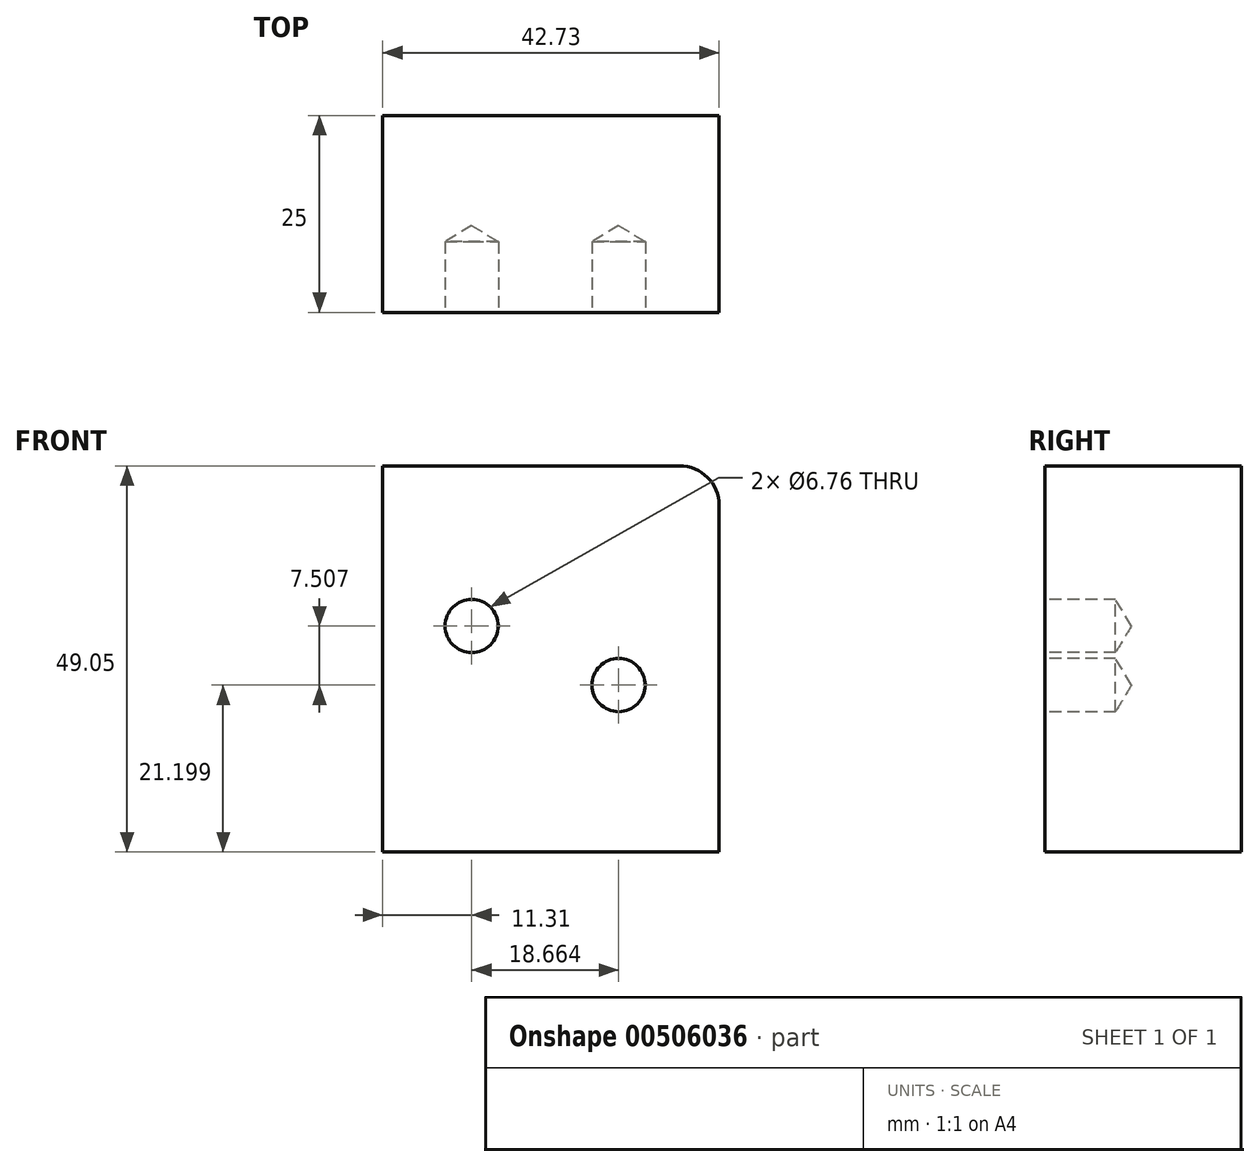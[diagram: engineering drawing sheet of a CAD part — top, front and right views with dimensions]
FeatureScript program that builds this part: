
annotation { "Feature Type Name" : "Feature", "Feature Type Description" : "" }
export const myFeature = defineFeature(function(context is Context, id is Id, definition is map)
    precondition{}
    {
        {
            var Q0;
            Q0=qCreatedBy(makeId("Front.planeOp"),FACE);
            var sketch = newSketch(context, id + "F0", { "sketchPlane" : qUnion([Q0])});
            skLineSegment(sketch, "E0.bottom", {"start": v(-90.46, 25.96) * mm, "end": v(-47.73, 25.96) * mm});
            skLineSegment(sketch, "E0.top", {"start": v(-90.46, 75) * mm, "end": v(-47.73, 75) * mm});
            skLineSegment(sketch, "E0.left", {"start": v(-90.46, 25.96) * mm, "end": v(-90.46, 75) * mm});
            skLineSegment(sketch, "E0.right", {"start": v(-47.73, 25.96) * mm, "end": v(-47.73, 75) * mm});
            skPoint(sketch, "E0.middle", {"position": v(-69.1, 50.48) * mm});
            skSolve(sketch);
        }
        {
            var Q0;
            Q0=makeQuery(id+"F0.imprint","IMPRINT",FACE,{"disambiguationData":[TD([[makeQuery(id+"F0.imprint","IMPRINT",EDGE,{"derivedFrom":sQuery(id+"F0.wireOp",EDGE,"E0.bottom")}),1.0]])]});
            extrude(context, id + "F1", {"entities" : qUnion([Q0]), "depth" : 25 * mm});
        }
        {
            var Q0;
            Q0=makeQuery(id+"F1.opExtrude","SWEPT_EDGE",EDGE,{"disambiguationData":[OSD([sQuery(id+"F0.wireOp",EDGE,"E0.top"),sQuery(id+"F0.wireOp",EDGE,"E0.right")])]});
            fillet(context, id + "F2", {"entities" : qUnion([Q0]), "radius" : 5 * mm, "tangentPropagation" : true, "allowEdgeOverflow" : false});
        }
        {
            var Q0;
            Q0=makeQuery(id+"F1.opExtrude","CAP_FACE",FACE,{"disambiguationData":[OSD([sQuery(id+"F0.wireOp",EDGE,"E0.bottom"),sQuery(id+"F0.wireOp",EDGE,"E0.top"),sQuery(id+"F0.wireOp",EDGE,"E0.left"),sQuery(id+"F0.wireOp",EDGE,"E0.right")])],"isStart":false});
            var sketch = newSketch(context, id + "F3", { "sketchPlane" : qUnion([Q0])});
            skPoint(sketch, "E1", {"position": v(-79.15, 54.67) * mm});
            skPoint(sketch, "E2", {"position": v(-60.49, 47.16) * mm});
            skSolve(sketch);
        }
        {
            var Q0;
            Q0=sQuery(id+"F3.wireOp",VERTEX,"E1");
            var Q1;
            Q1=sQuery(id+"F3.wireOp",VERTEX,"E2");
            var Q2;
            Q2=makeQuery(id+"F1.opExtrude","SWEPT_BODY",BODY,{"disambiguationData":[OSD([sQuery(id+"F0.wireOp",EDGE,"E0.bottom"),sQuery(id+"F0.wireOp",EDGE,"E0.top"),sQuery(id+"F0.wireOp",EDGE,"E0.left"),sQuery(id+"F0.wireOp",EDGE,"E0.right")])]});
            hole(context, id + "F4", {"style" : HoleStyle.SIMPLE, "endStyle" : HoleEndStyle.BLIND, "holeDiameter" : 6.76 * mm, "holeDepth" : 9 * mm, "isTappedThrough" : true, "tappedDepth" : 12 * mm, "tapClearance" : 3, "locations" : qUnion([Q0, Q1]), "scope" : qUnion([Q2])});
        }
    });
